# Revit family: Sink-Vessel-Lavatory-KOHLER-Kensho-K-8325
name_source: partatom
category: Plumbing Fixtures
revit_build: Autodesk Revit 2015 (Build: 20140606_1530(x64)
units: mm (PartAtom-declared; Revit-internal decimal feet)

## types (2) — shared parameters
ADA Compliant = No
Assembly Code = D2010400
CW Connection = No
Cold Water Inlet = Cold Water Inlet
Date Modified = 01/31/2019
Default Elevation = 36"
Description = Trough vessel bathroom sink
Drain Included = No
HW Connection = No
Height = 7 7/8"
Hot Water Inlet = Hot Water Inlet
Length = 27 15/16"
Manufacturer = KOHLER Co.
MasterFormat 1995 = 15410
MasterFormat 2004 = 22.41.16
Material = Natural Stone
Product Documentation Link = https://www.us.kohler.com
Product Name = Kensho
Product Page URL = http://www.us.kohler.com
URL = https://www.us.kohler.com
Vent Connection = No
Waste Connection = Yes
Waste Water Outlet = Waste Water Outlet
WaterSense Certified = No
Width = 14 1/16"

## per-type parameters (varying)
| type | Finish | Model | Type |
| CS6-Biancone | Kohler-Stone-CS6-Biancone | K-8325-CS6 | 1 |
| CS7-Grey Foussana | Kohler-Stone-CS7-Grey_Foussana | K-8325-CS7 | 2 |

## geometry (parser evidence)
native form markers: Sweep x4
no freeform markers — native parametric forms only
